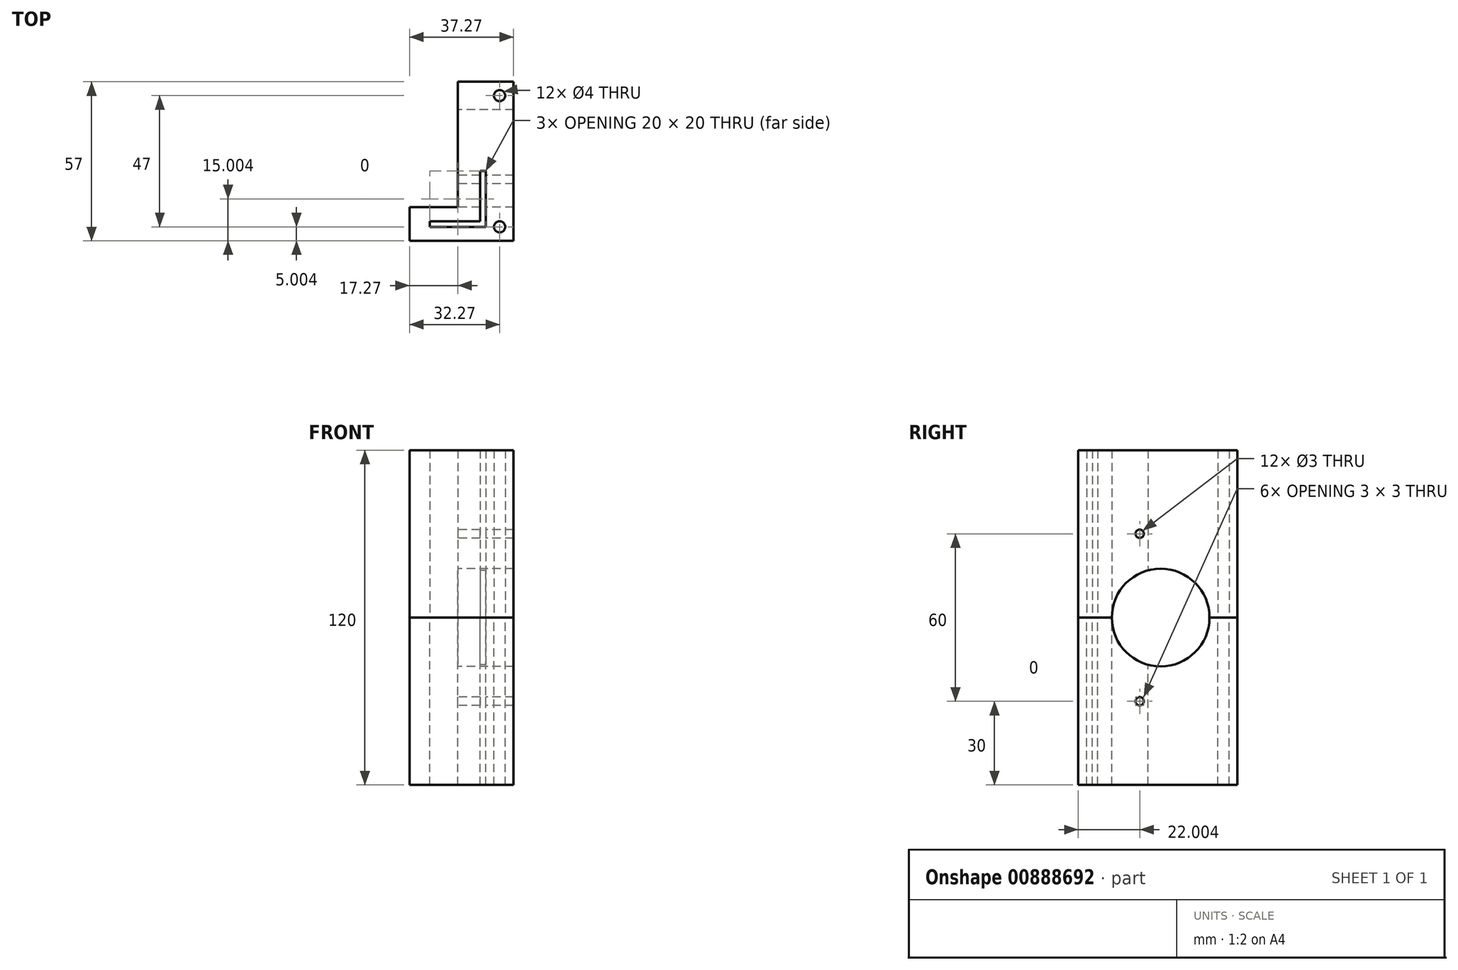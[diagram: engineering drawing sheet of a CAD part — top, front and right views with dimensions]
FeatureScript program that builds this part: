
annotation { "Feature Type Name" : "Feature", "Feature Type Description" : "" }
export const myFeature = defineFeature(function(context is Context, id is Id, definition is map)
    precondition{}
    {
        {
            var Q0;
            Q0=qCreatedBy(makeId("Top.planeOp"),FACE);
            var sketch = newSketch(context, id + "F0", { "sketchPlane" : qUnion([Q0])});
            skLineSegment(sketch, "E0", {"start": v(-20, 36.48) * mm, "end": v(0, 36.48) * mm});
            skLineSegment(sketch, "E1", {"start": v(0, 36.48) * mm, "end": v(0, -20.52) * mm});
            skLineSegment(sketch, "E2", {"start": v(0, -20.52) * mm, "end": v(-37.27, -20.52) * mm});
            skLineSegment(sketch, "E3", {"start": v(-37.27, -20.52) * mm, "end": v(-37.27, -8.52) * mm});
            skLineSegment(sketch, "E4", {"start": v(-37.27, -8.52) * mm, "end": v(-20, -8.52) * mm});
            skLineSegment(sketch, "E5", {"start": v(-20, -8.52) * mm, "end": v(-20, 36.48) * mm});
            skLineSegment(sketch, "E6", {"start": v(-10, 36.48) * mm, "end": v(-10, -20.52) * mm, "construction": true});
            skLineSegment(sketch, "E7", {"start": v(-30, -15.52) * mm, "end": v(-10, -15.52) * mm});
            skLineSegment(sketch, "E8", {"start": v(-10, -15.52) * mm, "end": v(-10, 4.48) * mm});
            skLineSegment(sketch, "E9", {"start": v(-10, 4.48) * mm, "end": v(-12, 4.48) * mm});
            skLineSegment(sketch, "E10", {"start": v(-12, 4.48) * mm, "end": v(-12, -13.52) * mm});
            skLineSegment(sketch, "E11", {"start": v(-12, -13.52) * mm, "end": v(-30, -13.52) * mm});
            skLineSegment(sketch, "E12", {"start": v(-30, -13.52) * mm, "end": v(-30, -15.52) * mm});
            skCircle(sketch, "E13", {"center": v(-5, -15.52) * mm, "radius": 2 * mm});
            skCircle(sketch, "E14", {"center": v(-5, 31.48) * mm, "radius": 2 * mm});
            skLineSegment(sketch, "E15", {"start": v(-5, -20.52) * mm, "end": v(-5, 36.48) * mm, "construction": true});
            skSolve(sketch);
        }
        {
            var Q0;
            Q0 = qSketchRegion(id + "F0", true);
            extrude(context, id + "F1", {"entities" : qUnion([Q0]), "depth" : 60 * mm, "offsetDistance" : 25 * mm});
        }
        {
            var Q0;
            Q0=makeQuery(id+"F1.opExtrude","SWEPT_FACE",FACE,{"disambiguationData":[OSD([sQuery(id+"F0.wireOp",EDGE,"E5")])]});
            var sketch = newSketch(context, id + "F2", { "sketchPlane" : qUnion([Q0])});
            skCircle(sketch, "E16", {"center": v(-1.48, 30) * mm, "radius": 1.5 * mm});
            skPoint(sketch, "E16.centerSnap0", {"position": v(8.52, 30) * mm});
            skCircle(sketch, "E17", {"center": v(-8.98, 0) * mm, "radius": 17.5 * mm});
            skLineSegment(sketch, "E18", {"start": v(-36.48, 30) * mm, "end": v(8.52, 30) * mm, "construction": true});
            skSolve(sketch);
        }
        {
            var Q0;
            Q0 = qSketchRegion(id + "F2", true);
            extrude(context, id + "F3", {"entities" : qUnion([Q0]), "operationType" : NewBodyOperationType.REMOVE, "endBound" : BoundingType.THROUGH_ALL, "oppositeDirection" : true, "depth" : 25 * mm, "offsetDistance" : 25 * mm});
        }
        {
            var Q0;
            Q0=makeQuery(id+"F1.opExtrude","SWEPT_BODY",BODY,{"disambiguationData":[OSD([sQuery(id+"F0.wireOp",EDGE,"E0"),sQuery(id+"F0.wireOp",EDGE,"E1"),sQuery(id+"F0.wireOp",EDGE,"E2"),sQuery(id+"F0.wireOp",EDGE,"E3"),sQuery(id+"F0.wireOp",EDGE,"E4"),sQuery(id+"F0.wireOp",EDGE,"E5"),sQuery(id+"F0.wireOp",EDGE,"E7"),sQuery(id+"F0.wireOp",EDGE,"E8"),sQuery(id+"F0.wireOp",EDGE,"E9"),sQuery(id+"F0.wireOp",EDGE,"E10"),sQuery(id+"F0.wireOp",EDGE,"E11"),sQuery(id+"F0.wireOp",EDGE,"E12"),sQuery(id+"F0.wireOp",EDGE,"E13"),sQuery(id+"F0.wireOp",EDGE,"E14")])]});
            var Q1;
            Q1=qCreatedBy(makeId("Top.planeOp"),FACE);
            mirror(context, id + "F4", {"entities" : qUnion([Q0]), "mirrorPlane" : qUnion([Q1])});
        }
    });
